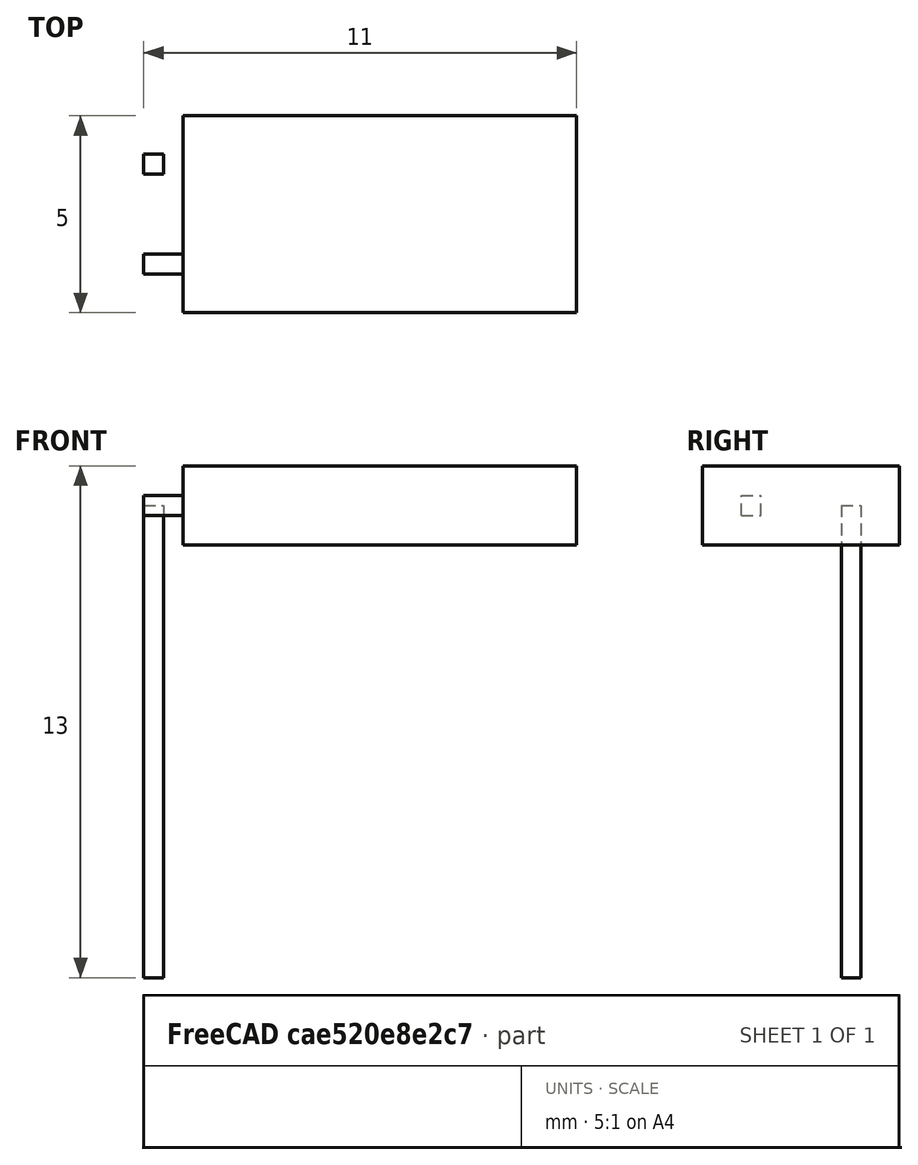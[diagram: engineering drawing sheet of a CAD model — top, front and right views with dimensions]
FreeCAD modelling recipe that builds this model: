
FCSTD DOCUMENT  (FreeCAD 0.16R)
Label: led_5x2_enchufable
License: All rights reserved
LicenseURL: http://en.wikipedia.org/wiki/All_rights_reserved
objects: Part::Box×3, Part::FeaturePython×2
note: 5 computed .brp shape members not serialized (recipe doc carries the construction recipe); baked Part::Feature solids carry a one-line shape summary decoded from their .brp

FEATURE [Part::Box] Box  label="Cube"
  Height = 2
  Length = 10
  Placement = pos=(-1,0,0) rot=(0,0,1;0rad)
  Width = 5
FEATURE [Part::Box] Box001  label="Cube001"
  Height = 0.5
  Length = 12
  Placement = pos=(-2,0.98,1) rot=(0,1,0;1.5708rad)
  Width = 0.5
FEATURE [Part::FeaturePython] Clone  label="Clone of Cube001"  # Draft clone (typed FeaturePython)
  Objects = -> [Box001]
  Placement = pos=(-2,3.52,1) rot=(0,1,0;1.5708rad)
  Scale = (1,1,1)
FEATURE [Part::Box] Box002  label="Cube002"
  Height = 0.5
  Length = 1
  Placement = pos=(-2,3.52,0.75) rot=(0,0,1;0rad)
  Width = 0.5
FEATURE [Part::FeaturePython] Clone001  label="Clone of Cube002"  # Draft clone (typed FeaturePython)
  Objects = -> [Box002]
  Placement = pos=(-2,0.98,0.75) rot=(0,0,1;0rad)
  Scale = (1,1,1)
